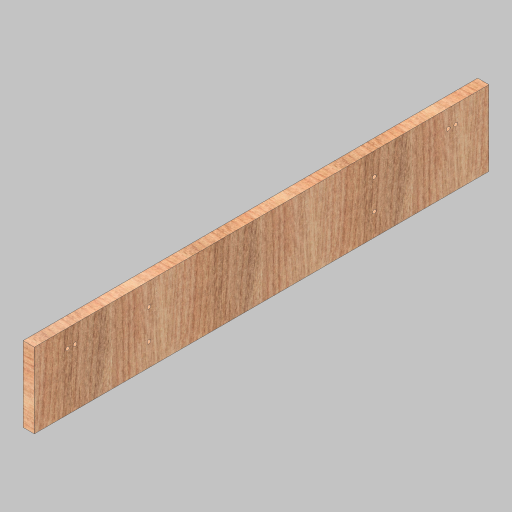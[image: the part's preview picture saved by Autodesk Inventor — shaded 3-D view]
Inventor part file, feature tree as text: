
AUTODESK INVENTOR PART (.ipt)
format: ipt  version: 2023.5 (Build 275446000, 446)  size: 230,912 bytes
history: native  units: in
note: dims shown in document units (in); Inventor stores cm internally (conversion verified against a paired STEP export)
features: sketch x2, extrude x1, hole x1
ambient origin geometry x8: Origin, YZ Plane, XZ Plane, XY Plane, X Axis, Y Axis, Z Axis, Center Point
bodies: Solid1 (feature_tree)
feature tree (4):
  extrude  "Extrusion1"  Depth=30.25in
  hole  "Hole1"  [1 undecoded]
  sketch  "Sketch1"  dims[d0=5.0in d1=30.25in]
  sketch  "Sketch2"  dims[d2=0.75in d3=0.0in d4=0.5in d5=2.211in d6=1.188in d7=0.25in d8=0.75in d9=0.375in d10=0.25in d11=0.5635in d12=1.0in d13=0.8108in d14=2.0in d16=7.625in]
note: 1 required parameter value undecoded (feature->parameter linkage not recoverable at this tier; creation-order binding heuristic only, values carry confidence <= 0.55)
